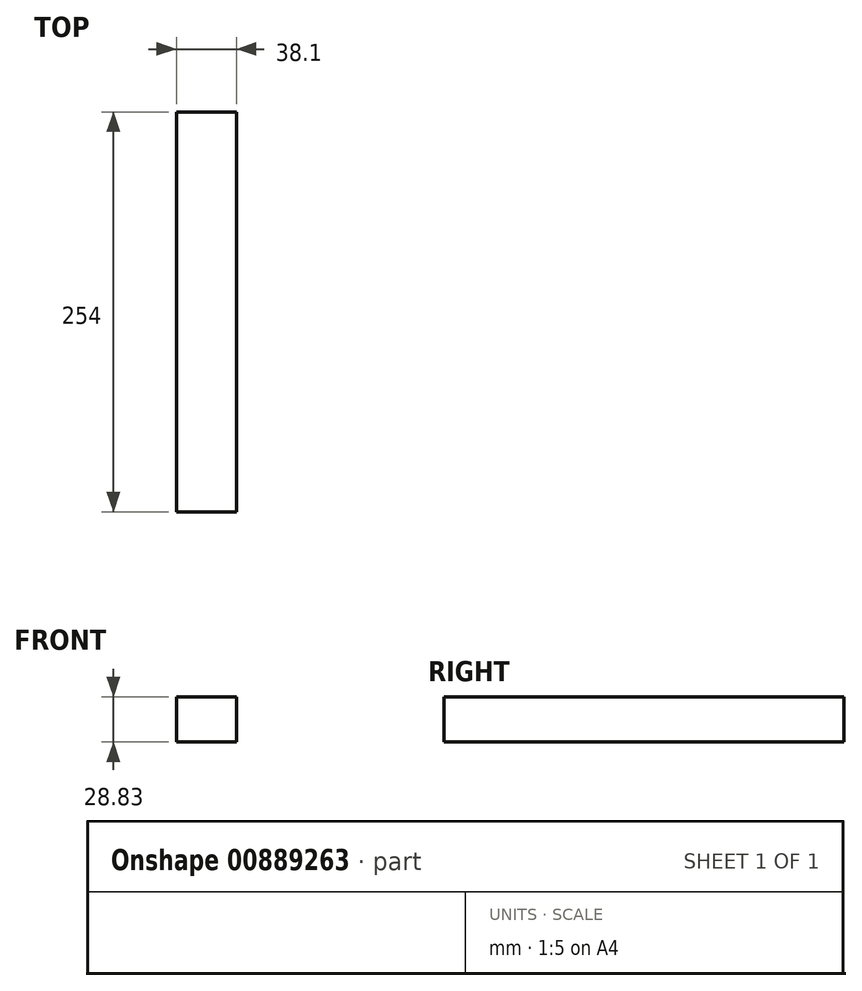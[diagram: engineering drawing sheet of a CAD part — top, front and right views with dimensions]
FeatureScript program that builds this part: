
annotation { "Feature Type Name" : "Feature", "Feature Type Description" : "" }
export const myFeature = defineFeature(function(context is Context, id is Id, definition is map)
    precondition{}
    {
        {
            var Q0;
            Q0=qCreatedBy(makeId("Front.planeOp"),FACE);
            var sketch = newSketch(context, id + "F0", { "sketchPlane" : qUnion([Q0])});
            skLineSegment(sketch, "E0.bottom", {"start": v(0, 0) * mm, "end": v(38.1, 0) * mm});
            skLineSegment(sketch, "E0.top", {"start": v(0, 28.83) * mm, "end": v(38.1, 28.83) * mm});
            skLineSegment(sketch, "E0.left", {"start": v(0, 0) * mm, "end": v(0, 28.83) * mm});
            skLineSegment(sketch, "E0.right", {"start": v(38.1, 0) * mm, "end": v(38.1, 28.83) * mm});
            skSolve(sketch);
        }
        {
            var Q0;
            Q0=makeQuery(id+"F0.imprint","IMPRINT",FACE,{"disambiguationData":[TD([[makeQuery(id+"F0.imprint","IMPRINT",EDGE,{"derivedFrom":sQuery(id+"F0.wireOp",EDGE,"E0.bottom")}),1.0]])]});
            extrude(context, id + "F1", {"entities" : qUnion([Q0]), "oppositeDirection" : true, "depth" : 254 * mm, "offsetDistance" : 25.4 * mm});
        }
    });
